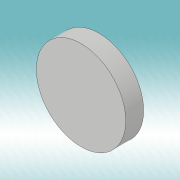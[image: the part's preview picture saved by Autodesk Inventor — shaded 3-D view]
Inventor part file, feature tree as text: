
AUTODESK INVENTOR PART (.ipt)
format: ipt  version: 2019 (Build 230136000, 136)  size: 88,576 bytes
history: native  units: mm
features: extrude x1, sketch x1
ambient origin geometry x8: Origin, YZ Plane, XZ Plane, XY Plane, X Axis, Y Axis, Z Axis, Center Point
bodies: Solid1 (feature_tree)
feature tree (2):
  extrude  "Extrusion1"  Depth=4.0mm TaperAngle=0.0deg
  sketch  "Sketch1"  dims[d0=20.0mm d1=4.0mm d2=0.0mm]
